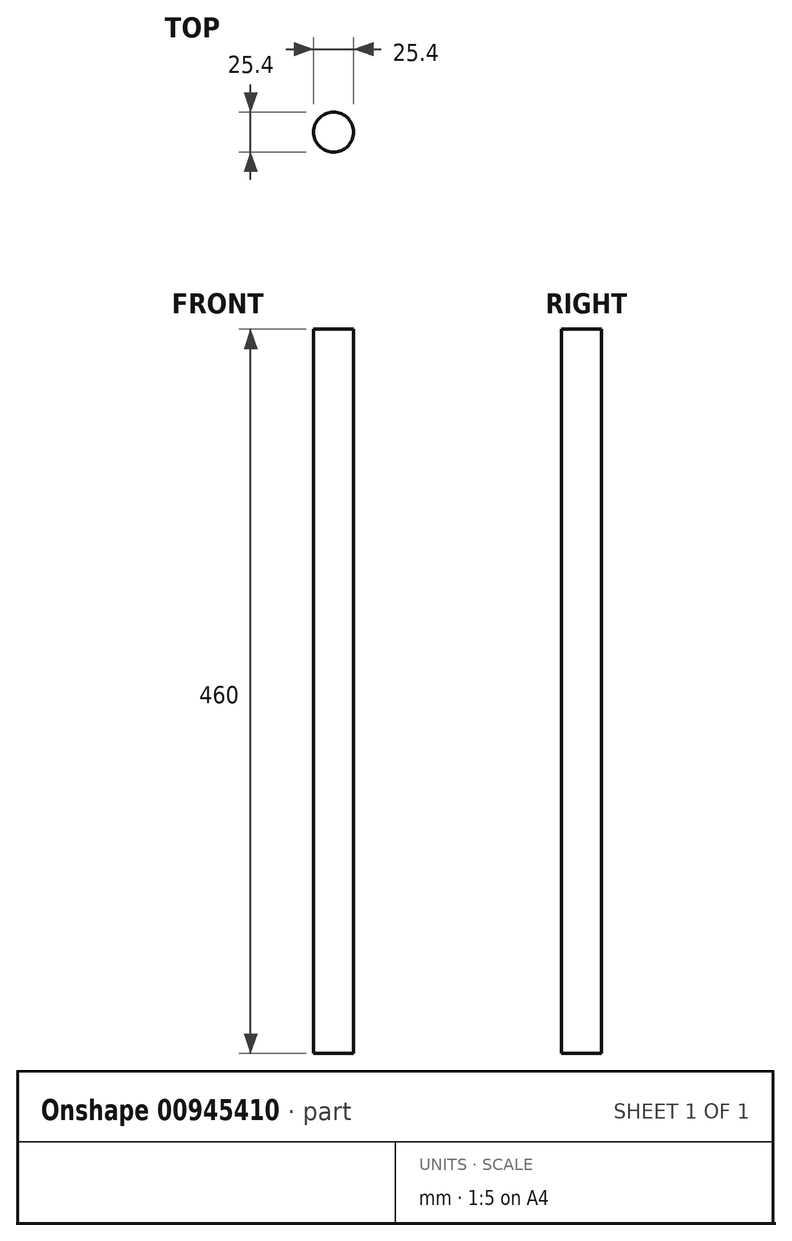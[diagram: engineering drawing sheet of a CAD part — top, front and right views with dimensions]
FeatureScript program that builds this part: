
annotation { "Feature Type Name" : "Feature", "Feature Type Description" : "" }
export const myFeature = defineFeature(function(context is Context, id is Id, definition is map)
    precondition{}
    {
        {
            var Q0;
            Q0=qCreatedBy(makeId("Top.planeOp"),FACE);
            var sketch = newSketch(context, id + "F0", { "sketchPlane" : qUnion([Q0])});
            skCircle(sketch, "E0", {"center": v(0, 0) * mm, "radius": 12.7 * mm});
            skSolve(sketch);
        }
        {
            var Q0;
            Q0=sQuery(id+"F0.wireOp",EDGE,"E0");
            extrude(context, id + "F1", {"bodyType" : ToolBodyType.SURFACE, "surfaceEntities" : qUnion([Q0]), "depth" : 460 * mm, "offsetDistance" : 25.4 * mm});
        }
    });
